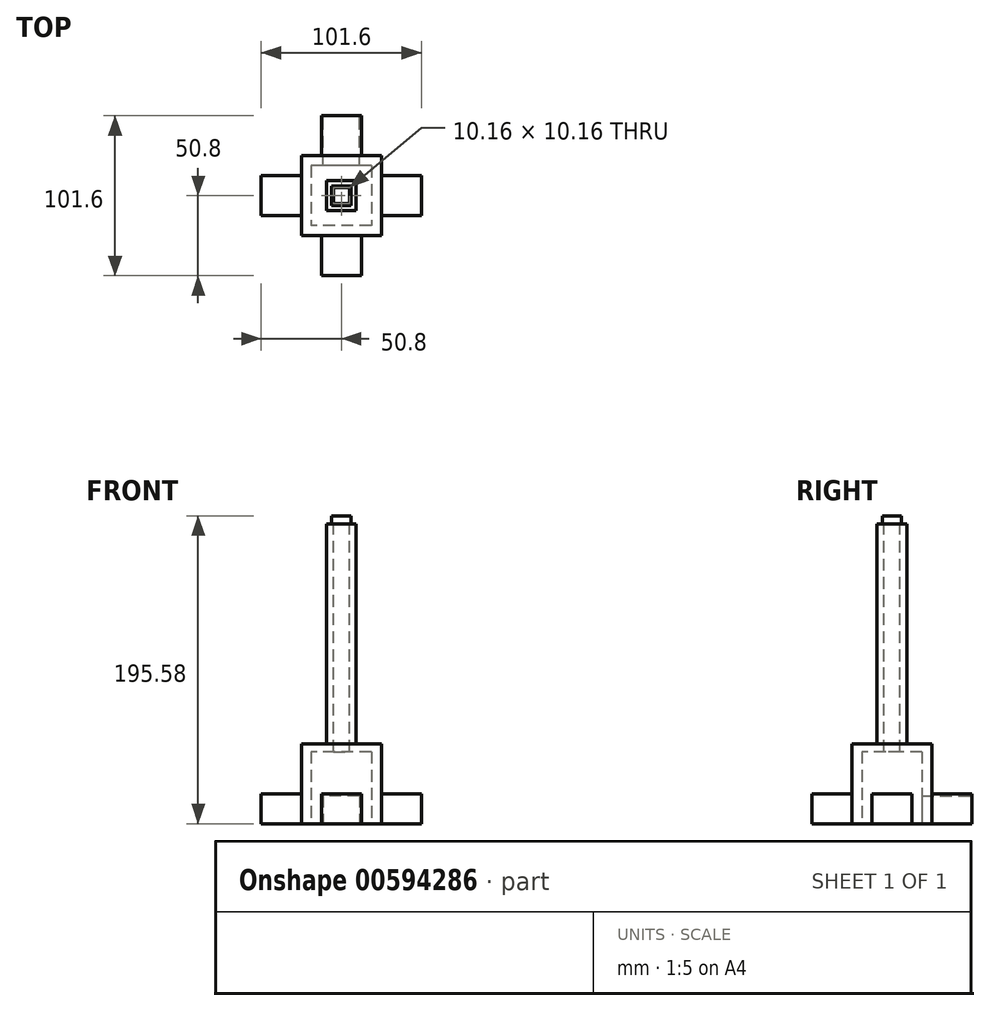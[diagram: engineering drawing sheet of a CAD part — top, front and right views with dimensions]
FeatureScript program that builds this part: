
annotation { "Feature Type Name" : "Feature", "Feature Type Description" : "" }
export const myFeature = defineFeature(function(context is Context, id is Id, definition is map)
    precondition{}
    {
        {
            var Q0;
            Q0=qCreatedBy(makeId("Top.planeOp"),FACE);
            var sketch = newSketch(context, id + "F0", { "sketchPlane" : qUnion([Q0])});
            skLineSegment(sketch, "E0.bottom", {"start": v(25.4, -25.4) * mm, "end": v(-25.4, -25.4) * mm});
            skLineSegment(sketch, "E0.top", {"start": v(25.4, 25.4) * mm, "end": v(-25.4, 25.4) * mm});
            skLineSegment(sketch, "E0.left", {"start": v(25.4, -25.4) * mm, "end": v(25.4, 25.4) * mm});
            skLineSegment(sketch, "E0.right", {"start": v(-25.4, -25.4) * mm, "end": v(-25.4, 25.4) * mm});
            skPoint(sketch, "E0.middle", {"position": v(0, 0) * mm});
            skSolve(sketch);
        }
        {
            var Q0;
            Q0 = qSketchRegion(id + "F0", true);
            extrude(context, id + "F1", {"entities" : qUnion([Q0]), "depth" : 50.8 * mm, "offsetDistance" : 25.4 * mm});
        }
        {
            var Q0;
            Q0=makeQuery(id+"F1.opExtrude","CAP_FACE",FACE,{"disambiguationData":[OSD([sQuery(id+"F0.wireOp",EDGE,"E0.bottom"),sQuery(id+"F0.wireOp",EDGE,"E0.top"),sQuery(id+"F0.wireOp",EDGE,"E0.left"),sQuery(id+"F0.wireOp",EDGE,"E0.right")])],"isStart":true});
            var sketch = newSketch(context, id + "F2", { "sketchPlane" : qUnion([Q0])});
            skLineSegment(sketch, "E1.bottom", {"start": v(19.05, -19.05) * mm, "end": v(-19.05, -19.05) * mm});
            skLineSegment(sketch, "E1.top", {"start": v(19.05, 19.05) * mm, "end": v(-19.05, 19.05) * mm});
            skLineSegment(sketch, "E1.left", {"start": v(19.05, -19.05) * mm, "end": v(19.05, 19.05) * mm});
            skLineSegment(sketch, "E1.right", {"start": v(-19.05, -19.05) * mm, "end": v(-19.05, 19.05) * mm});
            skPoint(sketch, "E1.middle", {"position": v(0, 0) * mm});
            skSolve(sketch);
        }
        {
            var Q0;
            Q0 = qSketchRegion(id + "F2", true);
            extrude(context, id + "F3", {"entities" : qUnion([Q0]), "operationType" : NewBodyOperationType.REMOVE, "oppositeDirection" : true, "depth" : 45.72 * mm, "offsetDistance" : 25.4 * mm});
        }
        {
            var Q0;
            Q0=makeQuery(id+"F1.opExtrude","CAP_FACE",FACE,{"disambiguationData":[OSD([sQuery(id+"F0.wireOp",EDGE,"E0.bottom"),sQuery(id+"F0.wireOp",EDGE,"E0.top"),sQuery(id+"F0.wireOp",EDGE,"E0.left"),sQuery(id+"F0.wireOp",EDGE,"E0.right")])],"isStart":false});
            var sketch = newSketch(context, id + "F4", { "sketchPlane" : qUnion([Q0])});
            skLineSegment(sketch, "E2.bottom", {"start": v(9.53, -9.52) * mm, "end": v(-9.53, -9.53) * mm});
            skLineSegment(sketch, "E2.top", {"start": v(9.53, 9.53) * mm, "end": v(-9.53, 9.52) * mm});
            skLineSegment(sketch, "E2.left", {"start": v(9.53, -9.52) * mm, "end": v(9.53, 9.53) * mm});
            skLineSegment(sketch, "E2.right", {"start": v(-9.53, -9.53) * mm, "end": v(-9.53, 9.52) * mm});
            skPoint(sketch, "E2.middle", {"position": v(0, 0) * mm});
            skSolve(sketch);
        }
        {
            var Q0;
            Q0 = qSketchRegion(id + "F4", true);
            extrude(context, id + "F5", {"entities" : qUnion([Q0]), "operationType" : NewBodyOperationType.ADD, "depth" : 139.7 * mm, "offsetDistance" : 25.4 * mm});
        }
        {
            var Q0;
            Q0=makeQuery(id+"F5.opExtrude","CAP_FACE",FACE,{"disambiguationData":[OSD([sQuery(id+"F4.wireOp",EDGE,"E2.bottom"),sQuery(id+"F4.wireOp",EDGE,"E2.top"),sQuery(id+"F4.wireOp",EDGE,"E2.left"),sQuery(id+"F4.wireOp",EDGE,"E2.right")])],"isStart":false});
            var sketch = newSketch(context, id + "F6", { "sketchPlane" : qUnion([Q0])});
            skLineSegment(sketch, "E3.bottom", {"start": v(6.1, -6.1) * mm, "end": v(-6.1, -6.1) * mm});
            skLineSegment(sketch, "E3.top", {"start": v(6.1, 6.1) * mm, "end": v(-6.1, 6.1) * mm});
            skLineSegment(sketch, "E3.left", {"start": v(6.1, -6.1) * mm, "end": v(6.1, 6.1) * mm});
            skLineSegment(sketch, "E3.right", {"start": v(-6.1, -6.1) * mm, "end": v(-6.1, 6.1) * mm});
            skPoint(sketch, "E3.middle", {"position": v(0, 0) * mm});
            skSolve(sketch);
        }
        {
            var Q0;
            Q0 = qSketchRegion(id + "F6", true);
            extrude(context, id + "F7", {"entities" : qUnion([Q0]), "operationType" : NewBodyOperationType.ADD, "depth" : 5.08 * mm, "offsetDistance" : 25.4 * mm});
        }
        {
            var Q0;
            Q0=makeQuery(id+"F7.opExtrude","CAP_FACE",FACE,{"disambiguationData":[OSD([sQuery(id+"F6.wireOp",EDGE,"E3.bottom"),sQuery(id+"F6.wireOp",EDGE,"E3.top"),sQuery(id+"F6.wireOp",EDGE,"E3.left"),sQuery(id+"F6.wireOp",EDGE,"E3.right")])],"isStart":false});
            var sketch = newSketch(context, id + "F8", { "sketchPlane" : qUnion([Q0])});
            skLineSegment(sketch, "E4.bottom", {"start": v(5.08, -5.08) * mm, "end": v(-5.08, -5.08) * mm});
            skLineSegment(sketch, "E4.top", {"start": v(5.08, 5.08) * mm, "end": v(-5.08, 5.08) * mm});
            skLineSegment(sketch, "E4.left", {"start": v(5.08, -5.08) * mm, "end": v(5.08, 5.08) * mm});
            skLineSegment(sketch, "E4.right", {"start": v(-5.08, -5.08) * mm, "end": v(-5.08, 5.08) * mm});
            skPoint(sketch, "E4.middle", {"position": v(0, 0) * mm});
            skSolve(sketch);
        }
        {
            var Q0;
            Q0=makeQuery(id+"F8.imprint","IMPRINT",FACE,{"disambiguationData":[TD([[makeQuery(id+"F8.imprint","IMPRINT",EDGE,{"derivedFrom":sQuery(id+"F8.wireOp",EDGE,"E4.bottom")}),-1.0]])]});
            var Q1;
            Q1 = qSketchRegion(id + "F8", true);
            extrude(context, id + "F9", {"entities" : qUnion([Q0, Q1]), "operationType" : NewBodyOperationType.REMOVE, "endBound" : BoundingType.THROUGH_ALL, "oppositeDirection" : true, "depth" : 25.4 * mm, "offsetDistance" : 25.4 * mm});
        }
        {
            var Q0;
            Q0=makeQuery(id+"F1.opExtrude","SWEPT_FACE",FACE,{"disambiguationData":[OSD([sQuery(id+"F0.wireOp",EDGE,"E0.bottom")])]});
            var sketch = newSketch(context, id + "F10", { "sketchPlane" : qUnion([Q0])});
            skLineSegment(sketch, "E5.bottom", {"start": v(12.7, 0) * mm, "end": v(-12.7, 0) * mm});
            skLineSegment(sketch, "E5.top", {"start": v(12.7, 19.05) * mm, "end": v(-12.7, 19.05) * mm});
            skLineSegment(sketch, "E5.left", {"start": v(12.7, 0) * mm, "end": v(12.7, 19.05) * mm});
            skLineSegment(sketch, "E5.right", {"start": v(-12.7, 0) * mm, "end": v(-12.7, 19.05) * mm});
            skPoint(sketch, "E5.middle", {"position": v(0, 9.53) * mm});
            skSolve(sketch);
        }
        {
            var Q0;
            Q0 = qSketchRegion(id + "F10", true);
            extrude(context, id + "F11", {"entities" : qUnion([Q0]), "operationType" : NewBodyOperationType.ADD, "depth" : 25.4 * mm, "offsetDistance" : 25.4 * mm});
        }
        {
            var Q0;
            Q0=makeQuery(id+"F1.opExtrude","SWEPT_FACE",FACE,{"disambiguationData":[OSD([sQuery(id+"F0.wireOp",EDGE,"E0.left")])]});
            var sketch = newSketch(context, id + "F12", { "sketchPlane" : qUnion([Q0])});
            skLineSegment(sketch, "E6.bottom", {"start": v(12.7, 0) * mm, "end": v(-12.7, 0) * mm});
            skLineSegment(sketch, "E6.top", {"start": v(12.7, 19.05) * mm, "end": v(-12.7, 19.05) * mm});
            skLineSegment(sketch, "E6.left", {"start": v(12.7, 0) * mm, "end": v(12.7, 19.05) * mm});
            skLineSegment(sketch, "E6.right", {"start": v(-12.7, 0) * mm, "end": v(-12.7, 19.05) * mm});
            skPoint(sketch, "E6.middle", {"position": v(0, 9.52) * mm});
            skSolve(sketch);
        }
        {
            var Q0;
            Q0 = qSketchRegion(id + "F12", true);
            extrude(context, id + "F13", {"entities" : qUnion([Q0]), "operationType" : NewBodyOperationType.ADD, "depth" : 25.4 * mm, "offsetDistance" : 25.4 * mm});
        }
        {
            var Q0;
            Q0=makeQuery(id+"F1.opExtrude","SWEPT_FACE",FACE,{"disambiguationData":[OSD([sQuery(id+"F0.wireOp",EDGE,"E0.right")])]});
            var sketch = newSketch(context, id + "F14", { "sketchPlane" : qUnion([Q0])});
            skLineSegment(sketch, "E7.bottom", {"start": v(12.7, 0) * mm, "end": v(-12.7, 0) * mm});
            skLineSegment(sketch, "E7.top", {"start": v(12.7, 19.05) * mm, "end": v(-12.7, 19.05) * mm});
            skLineSegment(sketch, "E7.left", {"start": v(12.7, 0) * mm, "end": v(12.7, 19.05) * mm});
            skLineSegment(sketch, "E7.right", {"start": v(-12.7, 0) * mm, "end": v(-12.7, 19.05) * mm});
            skPoint(sketch, "E7.middle", {"position": v(0, 9.53) * mm});
            skSolve(sketch);
        }
        {
            var Q0;
            Q0 = qSketchRegion(id + "F14", true);
            var Q1;
            Q1=makeQuery(id+"F14.imprint","IMPRINT",FACE,{"disambiguationData":[TD([[makeQuery(id+"F14.imprint","IMPRINT",EDGE,{"derivedFrom":sQuery(id+"F14.wireOp",EDGE,"E7.bottom")}),-1.0]])]});
            extrude(context, id + "F15", {"entities" : qUnion([Q0, Q1]), "operationType" : NewBodyOperationType.ADD, "depth" : 25.4 * mm, "offsetDistance" : 25.4 * mm});
        }
        {
            var Q0;
            Q0=makeQuery(id+"F1.opExtrude","SWEPT_FACE",FACE,{"disambiguationData":[OSD([sQuery(id+"F0.wireOp",EDGE,"E0.top")])]});
            var sketch = newSketch(context, id + "F16", { "sketchPlane" : qUnion([Q0])});
            skLineSegment(sketch, "E8.bottom", {"start": v(12.7, 0) * mm, "end": v(-12.7, 0) * mm});
            skLineSegment(sketch, "E8.top", {"start": v(12.7, 19.05) * mm, "end": v(-12.7, 19.05) * mm});
            skLineSegment(sketch, "E8.left", {"start": v(12.7, 0) * mm, "end": v(12.7, 19.05) * mm});
            skLineSegment(sketch, "E8.right", {"start": v(-12.7, 0) * mm, "end": v(-12.7, 19.05) * mm});
            skPoint(sketch, "E8.middle", {"position": v(0, 9.53) * mm});
            skSolve(sketch);
        }
        {
            var Q0;
            Q0 = qSketchRegion(id + "F16", true);
            extrude(context, id + "F17", {"entities" : qUnion([Q0]), "operationType" : NewBodyOperationType.ADD, "depth" : 25.4 * mm, "offsetDistance" : 25.4 * mm});
        }
        {
            var Q0;
            Q0=makeQuery(id+"F17.opExtrude","CAP_FACE",FACE,{"disambiguationData":[OSD([sQuery(id+"F16.wireOp",EDGE,"E8.bottom"),sQuery(id+"F16.wireOp",EDGE,"E8.top"),sQuery(id+"F16.wireOp",EDGE,"E8.left"),sQuery(id+"F16.wireOp",EDGE,"E8.right")])],"isStart":false});
            var sketch = newSketch(context, id + "F18", { "sketchPlane" : qUnion([Q0])});
            skLineSegment(sketch, "E9.bottom", {"start": v(11.43, 0) * mm, "end": v(-11.43, 0) * mm});
            skLineSegment(sketch, "E9.top", {"start": v(11.43, 17.78) * mm, "end": v(-11.43, 17.78) * mm});
            skLineSegment(sketch, "E9.left", {"start": v(11.43, 0) * mm, "end": v(11.43, 17.78) * mm});
            skLineSegment(sketch, "E9.right", {"start": v(-11.43, 0) * mm, "end": v(-11.43, 17.78) * mm});
            skPoint(sketch, "E9.middle", {"position": v(0, 8.9) * mm});
            skSolve(sketch);
        }
        {
            var Q0;
            Q0=makeQuery(id+"F18.imprint","IMPRINT",FACE,{"disambiguationData":[TD([[makeQuery(id+"F18.imprint","IMPRINT",EDGE,{"derivedFrom":sQuery(id+"F18.wireOp",EDGE,"E9.bottom")}),1.0]])]});
            extrude(context, id + "F19", {"entities" : qUnion([Q0]), "operationType" : NewBodyOperationType.REMOVE, "oppositeDirection" : true, "depth" : 38.1 * mm, "offsetDistance" : 25.4 * mm});
        }
    });
